# Revit family: Valve_Trim-DXV-Modulus-D35120500_Series
name_source: partatom
category: Plumbing Fixtures
revit_build: Autodesk Revit 2014 (Build: 20130308_1515(x64)
units: mm (PartAtom-declared; Revit-internal decimal feet)

## types (7) — shared parameters
ADA Compliant = Yes
Assembly Code = D2010710
CW Connection = Yes
CWFU = 3
Cold Water Connection Diameter = 1/2"
Default Elevation = 44"
Description = DXV Modulus Pressure Balance Shower Valve Trim
HW Connection = Yes
HWFU = 3
Height = 4 1/8"
Hot Water Connection Diameter = 1/2"
Installation Type = Wall Mounted
Length = 7 7/16"
Manufacturer = DXV
Price = Prices may vary. Please consult Manufacturer Representative for most up-to-date price list.
Shower Rough Valve D35000500.191 = No
Tempered Water Connection Diameter = 1/2"
URL = https://www.dxv.com
Vent Connection = No
WFU = 4
Warranty Documentation Link = https://www.dxv.com
Waste Connection = No
Width = 4 1/8"

## per-type parameters (varying)
| type | Finish | Material | Product Documentation Link | Product Page URL |
| D35120500.100 | Metal-DXV-100-Polished Chrome | Metal-DXV-100-Polished Chrome | https://dxv01.blob.core.windows.net | https://www.dxv.com |
| D35120500.144 | Metal-DXV-144-Brushed Nickel | Metal-DXV-144-Brushed Nickel |  |  |
| D35120500.150 | Metal-DXV-150-Platinum Nickel | Metal-DXV-150-Platinum Nickel | https://dxv01.blob.core.windows.net | https://www.dxv.com |
| D35120500.243 | Metal-DXV-243-Matte Black | Metal-DXV-243-Matte Black | https://dxv01.blob.core.windows.net | https://www.dxv.com |
| D35120500RB.100 | Metal-DXV-100-Polished Chrome | Metal-DXV-100-Polished Chrome | https://dxv01.blob.core.windows.net | https://www.dxv.com |
| D35120500RB.144 | Metal-DXV-144-Brushed Nickel | Metal-DXV-144-Brushed Nickel | https://dxv01.blob.core.windows.net | https://www.dxv.com |
| D35120500RB.150 | Metal-DXV-150-Platinum Nickel | Metal-DXV-150-Platinum Nickel | https://dxv01.blob.core.windows.net | https://www.dxv.com |

note: column(s) folded — value = type name in every type: Model

## geometry (parser evidence)
native form markers: Sweep x3
no freeform markers — native parametric forms only
